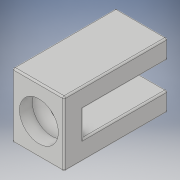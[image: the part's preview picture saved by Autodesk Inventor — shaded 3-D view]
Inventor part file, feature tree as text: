
AUTODESK INVENTOR PART (.ipt)
format: ipt  version: 2017 (Build 210142000, 142)  size: 150,528 bytes
history: native  units: in
note: dims shown in document units (in); Inventor stores cm internally (conversion verified against a paired STEP export)
features: sketch x3, hole x2, projected_geometry x2, extrude x1, fillet x1
ambient origin geometry x8: Origin, YZ Plane, XZ Plane, XY Plane, X Axis, Y Axis, Z Axis, Center Point
bodies: Solid1 (feature_tree)
feature tree (9):
  extrude  "Extrusion1"  Depth=0.25in
  fillet  "Fillet2"  Radius=0.1875in
  hole  "Hole1"  [1 undecoded]
  hole  "Hole2"  [1 undecoded]
  sketch  "Sketch1"  dims[d1=1.0in d4=0.25in d6=0.1875in]
  sketch  "Sketch6"  dims[d7=0.5in d8=0.0in d15=1.0in]
  projected_geometry  "Projected Loop5"
  sketch  "Sketch7"  dims[d22=0.1875in d24=0.1875in d29=0.015in d30=0.15in d31=0.75in d32=0.375in d33=0.25in d34=0.5635in d35=1.0in d36=0.8108in d37=0.375in d38=0.75in d39=0.375in d40=0.25in d41=0.5635in d42=0.125in d43=0.8108in]
  projected_geometry  "Projected Loop6"
note: 2 required parameter values undecoded (feature->parameter linkage not recoverable at this tier; creation-order binding heuristic only, values carry confidence <= 0.55)
